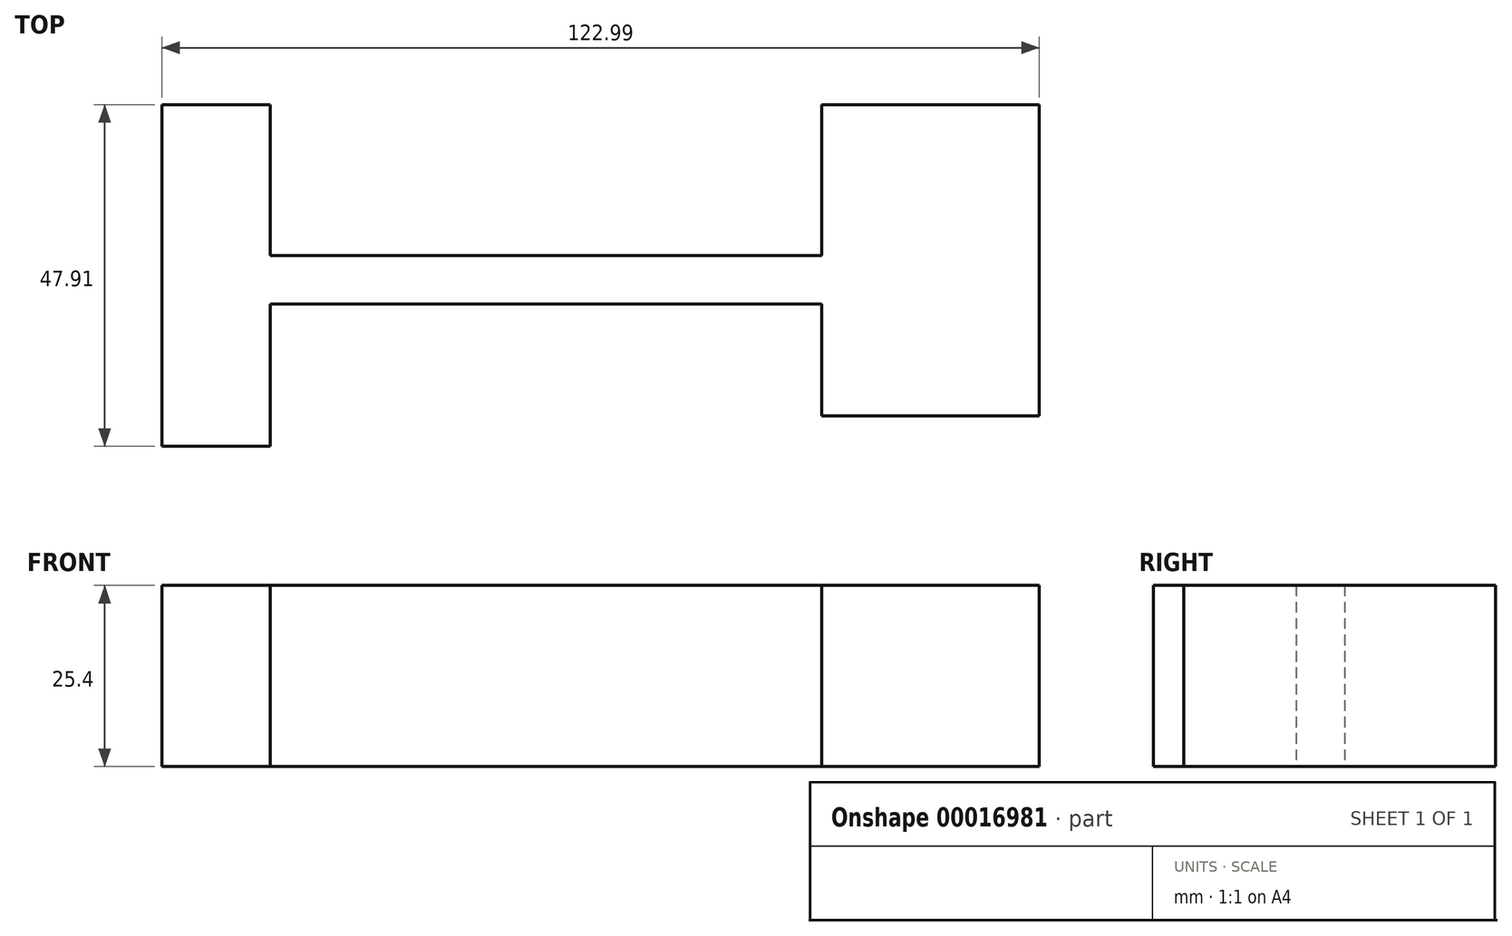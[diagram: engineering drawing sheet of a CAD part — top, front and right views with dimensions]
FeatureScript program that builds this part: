
annotation { "Feature Type Name" : "Feature", "Feature Type Description" : "" }
export const myFeature = defineFeature(function(context is Context, id is Id, definition is map)
    precondition{}
    {
        {
            var Q0;
            Q0=qCreatedBy(makeId("Top.planeOp"),FACE);
            var sketch = newSketch(context, id + "F0", { "sketchPlane" : qUnion([Q0])});
            skLineSegment(sketch, "E0", {"start": v(122.99, -43.66) * mm, "end": v(122.99, 0) * mm});
            skLineSegment(sketch, "E1", {"start": v(92.5, 0) * mm, "end": v(92.5, -43.66) * mm});
            skLineSegment(sketch, "E2", {"start": v(92.5, -43.66) * mm, "end": v(122.99, -43.66) * mm});
            skLineSegment(sketch, "E3", {"start": v(122.99, 0) * mm, "end": v(92.5, 0) * mm});
            skLineSegment(sketch, "E4.bottom", {"start": v(92.5, -27.94) * mm, "end": v(15.18, -27.94) * mm});
            skLineSegment(sketch, "E4.top", {"start": v(92.5, -21.16) * mm, "end": v(15.18, -21.16) * mm});
            skLineSegment(sketch, "E4.left", {"start": v(92.5, -27.94) * mm, "end": v(92.5, -21.16) * mm});
            skLineSegment(sketch, "E4.right", {"start": v(15.18, -27.94) * mm, "end": v(15.18, -21.16) * mm});
            skLineSegment(sketch, "E5.bottom", {"start": v(15.18, -27.94) * mm, "end": v(0, -27.94) * mm});
            skLineSegment(sketch, "E5.top", {"start": v(15.18, 0) * mm, "end": v(0, 0) * mm});
            skLineSegment(sketch, "E5.left", {"start": v(15.18, -27.94) * mm, "end": v(15.18, 0) * mm});
            skLineSegment(sketch, "E5.right", {"start": v(0, -27.94) * mm, "end": v(0, 0) * mm});
            skLineSegment(sketch, "E6.bottom", {"start": v(15.18, -21.16) * mm, "end": v(0, -21.16) * mm});
            skLineSegment(sketch, "E6.top", {"start": v(15.18, -47.9) * mm, "end": v(0, -47.9) * mm});
            skLineSegment(sketch, "E6.left", {"start": v(15.18, -21.16) * mm, "end": v(15.18, -47.9) * mm});
            skLineSegment(sketch, "E6.right", {"start": v(0, -21.16) * mm, "end": v(0, -47.9) * mm});
            skSolve(sketch);
        }
        {
            var Q0;
            {var subQ2=sQuery(id+"F0.wireOp",EDGE,"E5.bottom");Q0=makeQuery(id+"F0.imprint","IMPRINT",FACE,{"disambiguationData":[TD([[makeQuery(id+"F0.imprint","IMPRINT",EDGE,{"derivedFrom":subQ2}),1.0]])]});}
            var Q1;
            Q1=makeQuery(id+"F0.imprint","IMPRINT",FACE,{"disambiguationData":[TD([[makeQuery(id+"F0.imprint","IMPRINT",EDGE,{"derivedFrom":sQuery(id+"F0.wireOp",EDGE,"E0")}),1.0]])]});
            var Q2;
            Q2=makeQuery(id+"F0.imprint","IMPRINT",FACE,{"disambiguationData":[TD([[makeQuery(id+"F0.imprint","IMPRINT",EDGE,{"derivedFrom":sQuery(id+"F0.wireOp",EDGE,"E5.top")}),1.0]])]});
            var Q3;
            {var subQ2=sQuery(id+"F0.wireOp",EDGE,"E4.bottom");Q3=makeQuery(id+"F0.imprint","IMPRINT",FACE,{"disambiguationData":[TD([[makeQuery(id+"F0.imprint","IMPRINT",EDGE,{"derivedFrom":subQ2}),-1.0]])]});}
            var Q4;
            {var subQ2=sQuery(id+"F0.wireOp",EDGE,"E5.bottom");Q4=makeQuery(id+"F0.imprint","IMPRINT",FACE,{"disambiguationData":[TD([[makeQuery(id+"F0.imprint","IMPRINT",EDGE,{"derivedFrom":subQ2}),-1.0]])]});}
            extrude(context, id + "F1", {"entities" : qUnion([Q0, Q1, Q2, Q3, Q4]), "depth" : 25.4 * mm});
        }
    });
